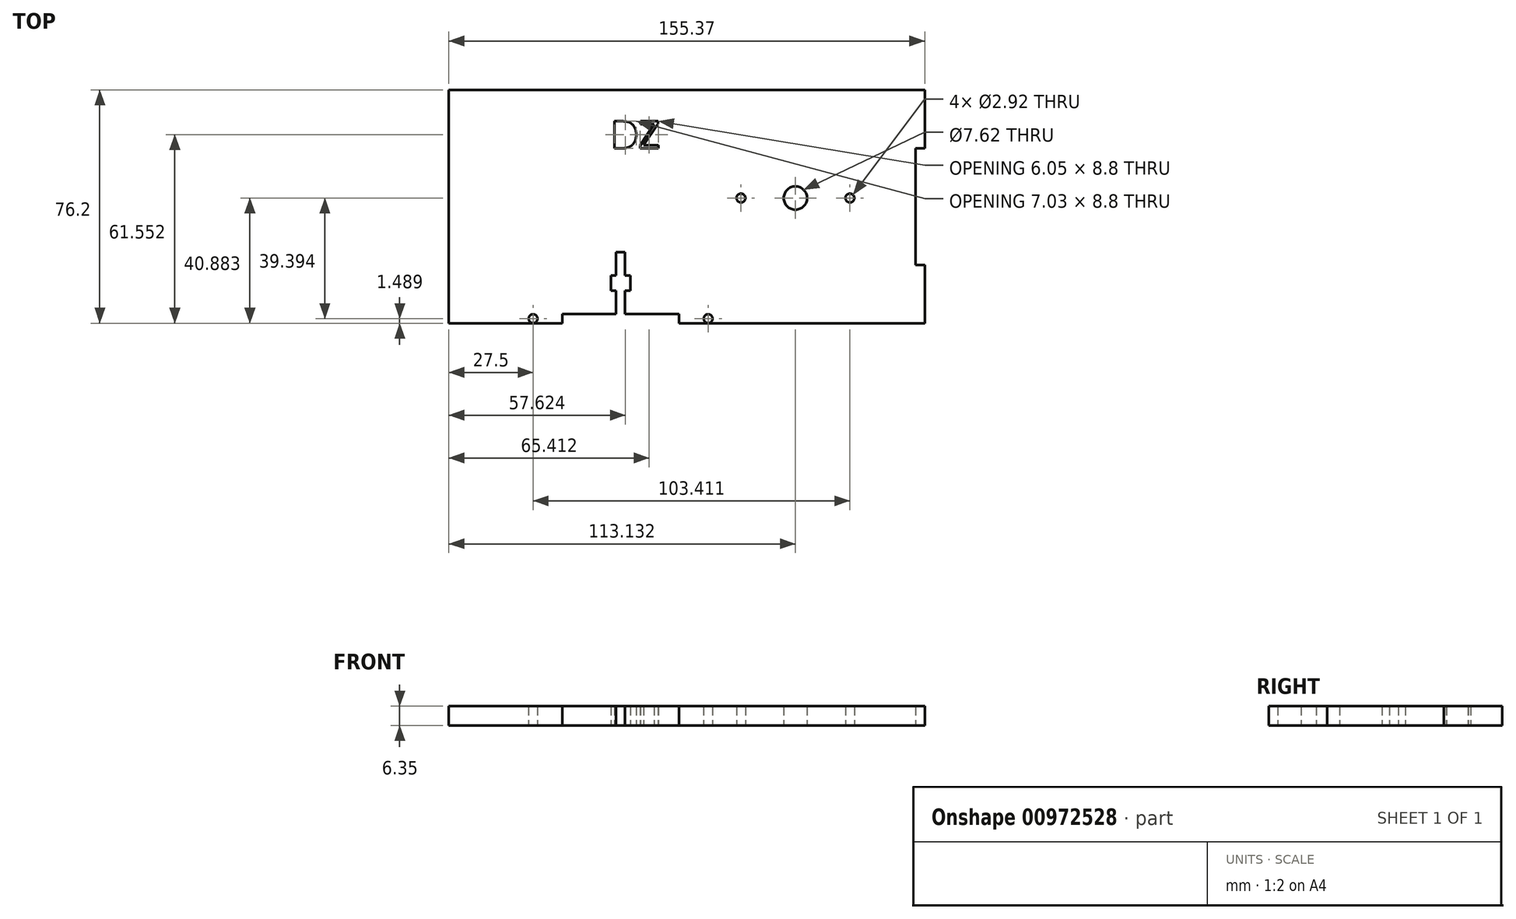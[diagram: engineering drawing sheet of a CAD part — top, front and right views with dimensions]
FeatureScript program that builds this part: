
annotation { "Feature Type Name" : "Feature", "Feature Type Description" : "" }
export const myFeature = defineFeature(function(context is Context, id is Id, definition is map)
    precondition{}
    {
        {
            var Q0;
            Q0=qCreatedBy(makeId("Top.planeOp"),FACE);
            var sketch = newSketch(context, id + "F0", { "sketchPlane" : qUnion([Q0])});
            skLineSegment(sketch, "E0.bottom", {"start": v(72.95, 28.18) * mm, "end": v(-82.42, 28.18) * mm});
            skLineSegment(sketch, "E0.top", {"start": v(72.95, -48.02) * mm, "end": v(-7.3, -48.02) * mm});
            skLineSegment(sketch, "E0.left", {"start": v(72.95, 28.18) * mm, "end": v(72.95, 9.13) * mm});
            skLineSegment(sketch, "E0.right", {"start": v(-82.42, 28.18) * mm, "end": v(-82.42, -48.02) * mm});
            skLineSegment(sketch, "E1", {"start": v(11.76, -48.02) * mm, "end": v(11.76, -45.04) * mm});
            skLineSegment(sketch, "E2", {"start": v(11.76, -48.02) * mm, "end": v(11.76, -45.04) * mm, "construction": true});
            skLineSegment(sketch, "E3", {"start": v(-7.3, -45.04) * mm, "end": v(-7.3, -48.02) * mm});
            skLineSegment(sketch, "E4", {"start": v(72.95, 9.13) * mm, "end": v(69.98, 9.13) * mm});
            skLineSegment(sketch, "E5", {"start": v(69.98, 9.13) * mm, "end": v(69.98, -28.97) * mm});
            skLineSegment(sketch, "E6", {"start": v(69.98, -28.97) * mm, "end": v(72.95, -28.97) * mm});
            skLineSegment(sketch, "E7", {"start": v(-26.34, -38.1) * mm, "end": v(-26.34, -1.45) * mm, "construction": true});
            skLineSegment(sketch, "E8", {"start": v(-7.3, -45.04) * mm, "end": v(-24.88, -45.04) * mm});
            skLineSegment(sketch, "E9", {"start": v(-24.88, -45.04) * mm, "end": v(-24.88, -37.42) * mm});
            skLineSegment(sketch, "E10", {"start": v(-24.88, -37.42) * mm, "end": v(-23.17, -37.42) * mm});
            skLineSegment(sketch, "E11", {"start": v(-23.17, -37.42) * mm, "end": v(-23.17, -32.47) * mm});
            skLineSegment(sketch, "E12", {"start": v(-23.17, -32.47) * mm, "end": v(-24.88, -32.47) * mm});
            skLineSegment(sketch, "E13", {"start": v(-24.88, -32.47) * mm, "end": v(-24.88, -24.85) * mm});
            skLineSegment(sketch, "E14", {"start": v(-24.88, -24.85) * mm, "end": v(-26.34, -24.85) * mm});
            skLineSegment(sketch, "E15.MirrorCS", {"start": v(-27.8, -24.85) * mm, "end": v(-26.34, -24.85) * mm});
            skLineSegment(sketch, "E16.MirrorCS", {"start": v(-27.8, -32.47) * mm, "end": v(-27.8, -24.85) * mm});
            skLineSegment(sketch, "E17.MirrorCS", {"start": v(-29.52, -32.47) * mm, "end": v(-27.8, -32.47) * mm});
            skLineSegment(sketch, "E18.MirrorCS", {"start": v(-29.52, -37.42) * mm, "end": v(-29.52, -32.47) * mm});
            skLineSegment(sketch, "E19.MirrorCS", {"start": v(-27.8, -37.42) * mm, "end": v(-29.52, -37.42) * mm});
            skLineSegment(sketch, "E20.MirrorCS", {"start": v(-27.8, -45.04) * mm, "end": v(-27.8, -37.42) * mm});
            skLineSegment(sketch, "E21.MirrorCS", {"start": v(-45.4, -45.04) * mm, "end": v(-27.8, -45.04) * mm});
            skLineSegment(sketch, "E22.MirrorCS", {"start": v(-26.34, -51.99) * mm, "end": v(-26.34, -88.64) * mm, "construction": true});
            skLineSegment(sketch, "E23.MirrorCS", {"start": v(-45.4, -45.04) * mm, "end": v(-45.4, -48.02) * mm});
            skLineSegment(sketch, "E24", {"start": v(2.23, -45.04) * mm, "end": v(2.23, -48.02) * mm, "construction": true});
            skCircle(sketch, "E25", {"center": v(2.23, -46.53) * mm, "radius": 1.46 * mm});
            skCircle(sketch, "E26.MirrorC", {"center": v(-54.92, -46.53) * mm, "radius": 1.46 * mm});
            skText(sketch, "E27", { "text": "DZ", "fontName": "OpenSans-Regular.ttf"});
            skLineSegment(sketch, "E28.trimOffspring", {"start": v(-45.4, -48.02) * mm, "end": v(-82.42, -48.02) * mm});
            skLineSegment(sketch, "E29.trimOffspring", {"start": v(72.95, -28.97) * mm, "end": v(72.95, -48.02) * mm});
            skPoint(sketch, "E30.end.orphan", {"position": v(69.98, 28.18) * mm});
            skPoint(sketch, "E31.orphan", {"position": v(-26.34, -45.04) * mm});
            skPoint(sketch, "E32.MirrorCS.end.orphan", {"position": v(-45.4, -45.04) * mm});
            skCircle(sketch, "E33", {"center": v(30.71, -7.14) * mm, "radius": 3.81 * mm});
            skLineSegment(sketch, "E34", {"start": v(30.71, -7.14) * mm, "end": v(48.5, -7.14) * mm, "construction": true});
            skLineSegment(sketch, "E35", {"start": v(30.71, -7.14) * mm, "end": v(12.93, -7.14) * mm, "construction": true});
            skCircle(sketch, "E36", {"center": v(48.5, -7.14) * mm, "radius": 1.46 * mm});
            skCircle(sketch, "E37", {"center": v(12.93, -7.14) * mm, "radius": 1.46 * mm});
            const initialGuessF0  = {"E27": [-0.02952, 0.00913, 1, 0, 0.00888]};
            skSetInitialGuess(sketch, initialGuessF0);
            skSolve(sketch);
        }
        {
            var Q0;
            {var subQ4=sQuery(id+"F0.wireOp",EDGE,"E2");Q0=makeQuery(id+"F0.imprint","IMPRINT",FACE,{"disambiguationData":[TD([[makeQuery(id+"F0.imprint","IMPRINT",EDGE,{"derivedFrom":subQ4}),-1.0]])]});}
            var Q1;
            {var subQ3=sQuery(id+"F0.wireOp",EDGE,"E32.MirrorCS");Q1=makeQuery(id+"F0.imprint","IMPRINT",FACE,{"disambiguationData":[TD([[makeQuery(id+"F0.imprint","IMPRINT",EDGE,{"derivedFrom":subQ3}),1.0]])]});}
            var Q2;
            {var subQ0=sQuery(id+"F0.wireOp",EDGE,"E8");var subQ4=sQuery(id+"F0.wireOp",EDGE,"E9");var subQ5=makeQuery(id+"F0.imprint","INTERSECT",VERTEX,{"derivedFrom":[subQ0,subQ4]});Q2=makeQuery(id+"F0.imprint","IMPRINT",FACE,{"disambiguationData":[TD([[makeQuery(id+"F0.imprint","IMPRINT",EDGE,{"disambiguationData":[TD([[subQ5,-1.0]])],"derivedFrom":subQ4}),-1.0]])]});}
            var Q3;
            Q3=makeQuery(id+"F0.imprint","IMPRINT",FACE,{"disambiguationData":[TD([[makeQuery(id+"F0.imprint","IMPRINT",EDGE,{"derivedFrom":sQuery(id+"F0.wireOp",EDGE,"E32.MirrorCS")}),-1.0]])]});
            var Q4;
            {var subQ0=sQuery(id+"F0.wireOp",EDGE,"E3");Q4=makeQuery(id+"F0.imprint","IMPRINT",FACE,{"disambiguationData":[TD([[makeQuery(id+"F0.imprint","IMPRINT",EDGE,{"derivedFrom":subQ0}),1.0]])]});}
            var Q5;
            {var subQ5=sQuery(id+"F0.wireOp",EDGE,"E2");Q5=makeQuery(id+"F0.imprint","IMPRINT",FACE,{"disambiguationData":[TD([[makeQuery(id+"F0.imprint","IMPRINT",EDGE,{"derivedFrom":subQ5}),1.0]])]});}
            var Q6;
            Q6=makeQuery(id+"F0.imprint","IMPRINT",FACE,{"disambiguationData":[TD([[makeQuery(id+"F0.imprint","IMPRINT",EDGE,{"derivedFrom":sQuery(id+"F0.wireOp",EDGE,"sU1DYdiF-OnwK-bo2G-owXp-GAfO8q8cCxOV")}),1.0]])]});
            extrude(context, id + "F1", {"entities" : qUnion([Q0, Q1, Q2, Q3, Q4, Q5, Q6]), "depth" : 6.35 * mm, "offsetDistance" : 25.4 * mm});
        }
    });
